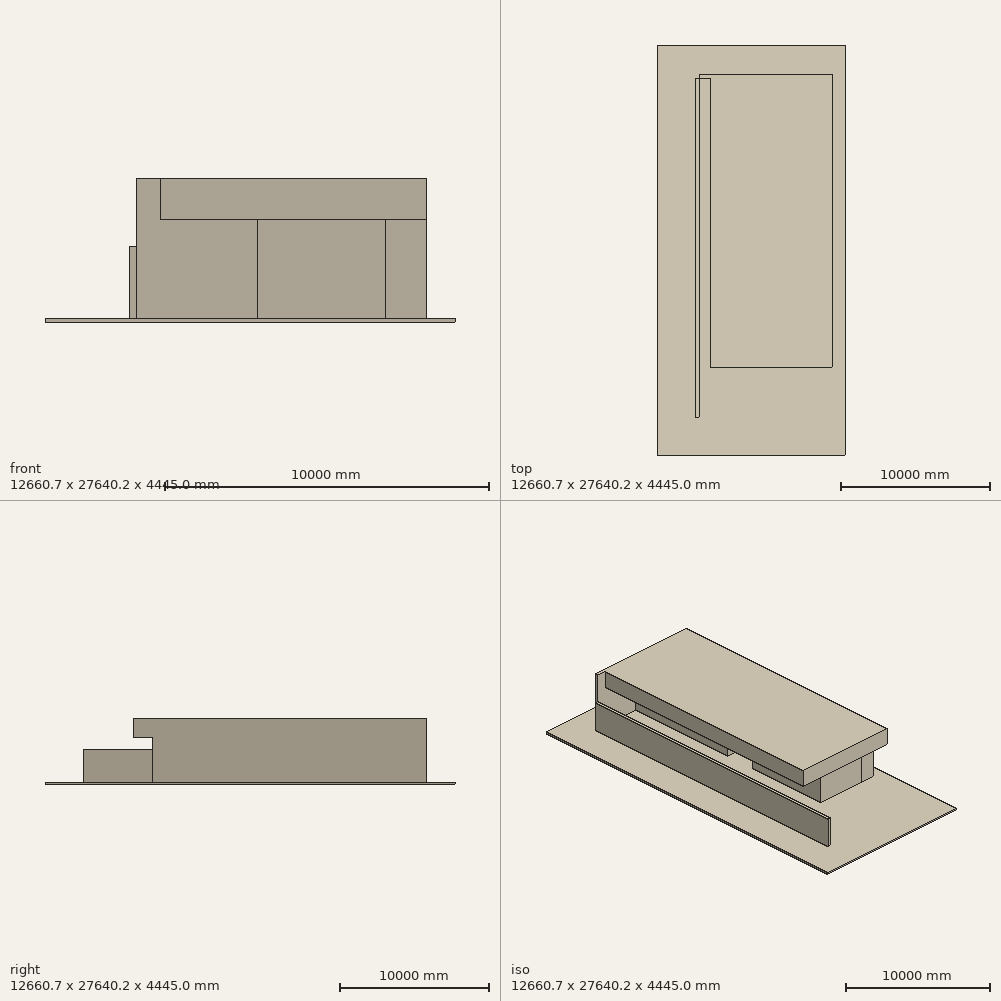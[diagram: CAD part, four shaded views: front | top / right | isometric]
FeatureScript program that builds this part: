
annotation { "Feature Type Name" : "Feature", "Feature Type Description" : "" }
export const myFeature = defineFeature(function(context is Context, id is Id, definition is map)
    precondition{}
    {
        {
            var Q0;
            Q0=qCreatedBy(makeId("Top.planeOp"),FACE);
            var sketch = newSketch(context, id + "F0", { "sketchPlane" : qUnion([Q0])});
            skLineSegment(sketch, "E0.bottom", {"start": v(0, 0) * mm, "end": v(3962.4, 0) * mm});
            skLineSegment(sketch, "E0.top", {"start": v(0, 9040.37) * mm, "end": v(100.58, 9040.37) * mm});
            skLineSegment(sketch, "E0.left", {"start": v(0, 0) * mm, "end": v(0, 9040.37) * mm});
            skLineSegment(sketch, "E0.right", {"start": v(3962.4, 0) * mm, "end": v(3962.4, 100.58) * mm});
            skLineSegment(sketch, "E1.bottom", {"start": v(0, -9144) * mm, "end": v(3962.4, -9144) * mm});
            skLineSegment(sketch, "E1.top", {"start": v(0, -2438.4) * mm, "end": v(3962.4, -2438.4) * mm});
            skLineSegment(sketch, "E1.left", {"start": v(0, -2438.4) * mm, "end": v(0, -9144) * mm});
            skLineSegment(sketch, "E1.right", {"start": v(3962.4, -2438.4) * mm, "end": v(3962.4, -9144) * mm});
            skLineSegment(sketch, "E2", {"start": v(100.58, 9040.37) * mm, "end": v(100.58, 100.58) * mm});
            skLineSegment(sketch, "E3", {"start": v(100.58, 100.58) * mm, "end": v(3962.4, 100.58) * mm});
            skSolve(sketch);
        }
        {
            var Q0;
            Q0 = qSketchRegion(id + "F0", true);
            extrude(context, id + "F1", {"entities" : qUnion([Q0]), "depth" : 3048 * mm});
        }
        {
            var Q0;
            Q0=qCreatedBy(makeId("Top.planeOp"),FACE);
            var sketch = newSketch(context, id + "F2", { "sketchPlane" : qUnion([Q0])});
            skLineSegment(sketch, "E4.bottom", {"start": v(-3718.56, 9040.37) * mm, "end": v(3962.4, 9040.37) * mm});
            skLineSegment(sketch, "E4.top", {"start": v(-3718.56, 9284.2) * mm, "end": v(3962.4, 9284.2) * mm});
            skLineSegment(sketch, "E4.left", {"start": v(-3718.56, 9040.37) * mm, "end": v(-3718.56, 9284.2) * mm});
            skLineSegment(sketch, "E4.right", {"start": v(3962.4, 9040.37) * mm, "end": v(3962.4, 9284.2) * mm});
            skLineSegment(sketch, "E5.bottom", {"start": v(-3718.56, 9040.37) * mm, "end": v(-3962.4, 9040.37) * mm});
            skLineSegment(sketch, "E5.top", {"start": v(-3718.56, -13819.63) * mm, "end": v(-3962.4, -13819.63) * mm});
            skLineSegment(sketch, "E5.left", {"start": v(-3718.56, 9040.37) * mm, "end": v(-3718.56, -13819.63) * mm});
            skLineSegment(sketch, "E5.right", {"start": v(-3962.4, 9040.37) * mm, "end": v(-3962.4, -13819.63) * mm});
            skSolve(sketch);
        }
        {
            var Q0;
            Q0 = qSketchRegion(id + "F2", true);
            extrude(context, id + "F3", {"entities" : qUnion([Q0]), "depth" : 2212.85 * mm});
        }
        {
            var Q0;
            Q0=makeQuery(id+"F1.opExtrude","CAP_FACE",FACE,{"disambiguationData":[OSD([sQuery(id+"F0.wireOp",EDGE,"E0.bottom"),sQuery(id+"F0.wireOp",EDGE,"E0.top"),sQuery(id+"F0.wireOp",EDGE,"E0.left"),sQuery(id+"F0.wireOp",EDGE,"E0.right")])],"isStart":false});
            var sketch = newSketch(context, id + "F4", { "sketchPlane" : qUnion([Q0])});
            skLineSegment(sketch, "E6.bottom", {"start": v(3962.4, 9284.2) * mm, "end": v(-2990.09, 9284.2) * mm});
            skLineSegment(sketch, "E6.top", {"start": v(3962.4, -10436.35) * mm, "end": v(-2990.09, -10436.35) * mm});
            skLineSegment(sketch, "E6.left", {"start": v(3962.4, 9284.2) * mm, "end": v(3962.4, -10436.35) * mm});
            skLineSegment(sketch, "E6.right", {"start": v(-2990.09, 9284.2) * mm, "end": v(-2990.09, -10436.35) * mm});
            skSolve(sketch);
        }
        {
            var Q0;
            Q0 = qSketchRegion(id + "F4", true);
            extrude(context, id + "F5", {"entities" : qUnion([Q0]), "depth" : 1270 * mm});
        }
        {
            var Q0;
            Q0=makeQuery(id+"F1.opExtrude","SWEPT_FACE",FACE,{"disambiguationData":[OSD([sQuery(id+"F0.wireOp",EDGE,"E1.right")])]});
            var sketch = newSketch(context, id + "F6", { "sketchPlane" : qUnion([Q0])});
            skLineSegment(sketch, "E7.bottom", {"start": v(-9144, 0) * mm, "end": v(9284.2, 0) * mm});
            skLineSegment(sketch, "E7.top", {"start": v(-9144, 4318) * mm, "end": v(9284.2, 4318) * mm});
            skLineSegment(sketch, "E7.left", {"start": v(-9144, 0) * mm, "end": v(-9144, 3048) * mm});
            skLineSegment(sketch, "E7.right", {"start": v(9284.2, 0) * mm, "end": v(9284.2, 4318) * mm});
            skLineSegment(sketch, "E8.bottom", {"start": v(-9144, 4318) * mm, "end": v(-10436.35, 4318) * mm});
            skLineSegment(sketch, "E8.top", {"start": v(-9144, 3048) * mm, "end": v(-10436.35, 3048) * mm});
            skLineSegment(sketch, "E8.right", {"start": v(-10436.35, 4318) * mm, "end": v(-10436.35, 3048) * mm});
            skSolve(sketch);
        }
        {
            var Q0;
            Q0 = qSketchRegion(id + "F6", true);
            extrude(context, id + "F7", {"entities" : qUnion([Q0]), "depth" : 1270 * mm});
        }
        {
            var Q0;
            Q0=qCreatedBy(makeId("Top.planeOp"),FACE);
            var sketch = newSketch(context, id + "F8", { "sketchPlane" : qUnion([Q0])});
            skLineSegment(sketch, "E9.bottom", {"start": v(6117.86, 11268.55) * mm, "end": v(-6542.87, 11268.55) * mm});
            skLineSegment(sketch, "E9.top", {"start": v(6117.86, -16371.62) * mm, "end": v(-6542.87, -16371.62) * mm});
            skLineSegment(sketch, "E9.left", {"start": v(6117.86, 11268.55) * mm, "end": v(6117.86, -16371.62) * mm});
            skLineSegment(sketch, "E9.right", {"start": v(-6542.87, 11268.55) * mm, "end": v(-6542.87, -16371.62) * mm});
            skSolve(sketch);
        }
        {
            var Q0;
            Q0 = qSketchRegion(id + "F8", true);
            extrude(context, id + "F9", {"entities" : qUnion([Q0]), "oppositeDirection" : true, "depth" : 127 * mm});
        }
        {
            var Q0;
            Q0=makeQuery(id+"F3.opExtrude","CAP_FACE",FACE,{"disambiguationData":[OSD([sQuery(id+"F2.wireOp",EDGE,"E4.bottom"),sQuery(id+"F2.wireOp",EDGE,"E4.top"),sQuery(id+"F2.wireOp",EDGE,"E4.left"),sQuery(id+"F2.wireOp",EDGE,"E4.right")])],"isStart":false});
            var sketch = newSketch(context, id + "F10", { "sketchPlane" : qUnion([Q0])});
            skLineSegment(sketch, "E10.bottom", {"start": v(-3718.56, 9284.2) * mm, "end": v(3962.4, 9284.2) * mm});
            skLineSegment(sketch, "E10.top", {"start": v(-3718.56, 9040.37) * mm, "end": v(3962.4, 9040.37) * mm});
            skLineSegment(sketch, "E10.left", {"start": v(-3718.56, 9284.2) * mm, "end": v(-3718.56, 9040.37) * mm});
            skLineSegment(sketch, "E10.right", {"start": v(3962.4, 9284.2) * mm, "end": v(3962.4, 9040.37) * mm});
            skSolve(sketch);
        }
        {
            var Q0;
            Q0 = qSketchRegion(id + "F10", true);
            var Q1;
            Q1=makeQuery(id+"F5.opExtrude","CAP_FACE",FACE,{"disambiguationData":[OSD([sQuery(id+"F4.wireOp",EDGE,"E6.bottom"),sQuery(id+"F4.wireOp",EDGE,"E6.top"),sQuery(id+"F4.wireOp",EDGE,"E6.left"),sQuery(id+"F4.wireOp",EDGE,"E6.right")])],"isStart":false});
            extrude(context, id + "F11", {"entities" : qUnion([Q0]), "operationType" : NewBodyOperationType.ADD, "endBound" : BoundingType.UP_TO_SURFACE, "endBoundEntityFace" : qUnion([Q1]), "depth" : 25.4 * mm});
        }
        {
            var Q0;
            Q0=qCreatedBy(makeId("Top.planeOp"),FACE);
            var sketch = newSketch(context, id + "F12", { "sketchPlane" : qUnion([Q0])});
            skLineSegment(sketch, "E11.bottom", {"start": v(1116.58, 608.58) * mm, "end": v(1891.28, 608.58) * mm});
            skLineSegment(sketch, "E11.top", {"start": v(1116.58, 1903.98) * mm, "end": v(1891.28, 1903.98) * mm});
            skLineSegment(sketch, "E11.left", {"start": v(1116.58, 608.58) * mm, "end": v(1116.58, 1903.98) * mm});
            skLineSegment(sketch, "E11.right", {"start": v(1891.28, 608.58) * mm, "end": v(1891.28, 1903.98) * mm});
            skLineSegment(sketch, "E12.bottom", {"start": v(1116.58, 2005.58) * mm, "end": v(1891.28, 2005.58) * mm});
            skLineSegment(sketch, "E12.top", {"start": v(1116.58, 3300.98) * mm, "end": v(1891.28, 3300.98) * mm});
            skLineSegment(sketch, "E12.left", {"start": v(1116.58, 2005.58) * mm, "end": v(1116.58, 3300.98) * mm});
            skLineSegment(sketch, "E12.right", {"start": v(1891.28, 2005.58) * mm, "end": v(1891.28, 3300.98) * mm});
            skLineSegment(sketch, "E13.bottom", {"start": v(1116.58, 3402.58) * mm, "end": v(1891.28, 3402.58) * mm});
            skLineSegment(sketch, "E13.top", {"start": v(1116.58, 4697.98) * mm, "end": v(1891.28, 4697.98) * mm});
            skLineSegment(sketch, "E13.left", {"start": v(1116.58, 3402.58) * mm, "end": v(1116.58, 4697.98) * mm});
            skLineSegment(sketch, "E13.right", {"start": v(1891.28, 3402.58) * mm, "end": v(1891.28, 4697.98) * mm});
            skLineSegment(sketch, "E14.bottom", {"start": v(2500.88, 4697.98) * mm, "end": v(3275.58, 4697.98) * mm});
            skLineSegment(sketch, "E14.top", {"start": v(2500.88, 3402.58) * mm, "end": v(3275.58, 3402.58) * mm});
            skLineSegment(sketch, "E14.left", {"start": v(2500.88, 4697.98) * mm, "end": v(2500.88, 3402.58) * mm});
            skLineSegment(sketch, "E14.right", {"start": v(3275.58, 4697.98) * mm, "end": v(3275.58, 3402.58) * mm});
            skLineSegment(sketch, "E15.bottom", {"start": v(2500.88, 3300.98) * mm, "end": v(3275.58, 3300.98) * mm});
            skLineSegment(sketch, "E15.top", {"start": v(2500.88, 2005.58) * mm, "end": v(3275.58, 2005.58) * mm});
            skLineSegment(sketch, "E15.left", {"start": v(2500.88, 3300.98) * mm, "end": v(2500.88, 2005.58) * mm});
            skLineSegment(sketch, "E15.right", {"start": v(3275.58, 3300.98) * mm, "end": v(3275.58, 2005.58) * mm});
            skLineSegment(sketch, "E16.bottom", {"start": v(2500.88, 1903.98) * mm, "end": v(3275.58, 1903.98) * mm});
            skLineSegment(sketch, "E16.top", {"start": v(2500.88, 608.58) * mm, "end": v(3275.58, 608.58) * mm});
            skLineSegment(sketch, "E16.left", {"start": v(2500.88, 1903.98) * mm, "end": v(2500.88, 608.58) * mm});
            skLineSegment(sketch, "E16.right", {"start": v(3275.58, 1903.98) * mm, "end": v(3275.58, 608.58) * mm});
            skLineSegment(sketch, "E17", {"start": v(1116.58, 3300.98) * mm, "end": v(1116.58, 3402.58) * mm, "construction": true});
            skLineSegment(sketch, "E18", {"start": v(1116.58, 1903.98) * mm, "end": v(1116.58, 2005.58) * mm, "construction": true});
            skSolve(sketch);
        }
        {
            var Q0;
            Q0 = qSketchRegion(id + "F12", true);
            extrude(context, id + "F13", {"entities" : qUnion([Q0]), "operationType" : NewBodyOperationType.ADD, "depth" : 1695.45 * mm});
        }
        {
            var Q0;
            Q0=qCreatedBy(makeId("Top.planeOp"),FACE);
            var sketch = newSketch(context, id + "F14", { "sketchPlane" : qUnion([Q0])});
            skLineSegment(sketch, "E19.bottom", {"start": v(607.65, 7254.54) * mm, "end": v(3668.35, 7254.54) * mm});
            skLineSegment(sketch, "E19.top", {"start": v(607.65, 5165.39) * mm, "end": v(3668.35, 5165.39) * mm});
            skLineSegment(sketch, "E19.left", {"start": v(607.65, 7254.54) * mm, "end": v(607.65, 5165.39) * mm});
            skLineSegment(sketch, "E19.right", {"start": v(3668.35, 7254.54) * mm, "end": v(3668.35, 5165.39) * mm});
            skSolve(sketch);
        }
        {
            var Q0;
            Q0 = qSketchRegion(id + "F14", true);
            extrude(context, id + "F15", {"entities" : qUnion([Q0]), "operationType" : NewBodyOperationType.ADD, "depth" : 1739.9 * mm});
        }
        {
            var Q0;
            Q0=qCreatedBy(makeId("Top.planeOp"),FACE);
            var sketch = newSketch(context, id + "F16", { "sketchPlane" : qUnion([Q0])});
            skLineSegment(sketch, "E20.bottom", {"start": v(1227.74, 8964) * mm, "end": v(478.44, 8964) * mm});
            skLineSegment(sketch, "E20.top", {"start": v(1227.74, 7363.8) * mm, "end": v(478.44, 7363.8) * mm});
            skLineSegment(sketch, "E20.left", {"start": v(1227.74, 8964) * mm, "end": v(1227.74, 7363.8) * mm});
            skLineSegment(sketch, "E20.right", {"start": v(478.44, 8964) * mm, "end": v(478.44, 7363.8) * mm});
            skSolve(sketch);
        }
        {
            var Q0;
            Q0 = qSketchRegion(id + "F16", true);
            extrude(context, id + "F17", {"entities" : qUnion([Q0]), "depth" : 1447.8 * mm});
        }
    });
